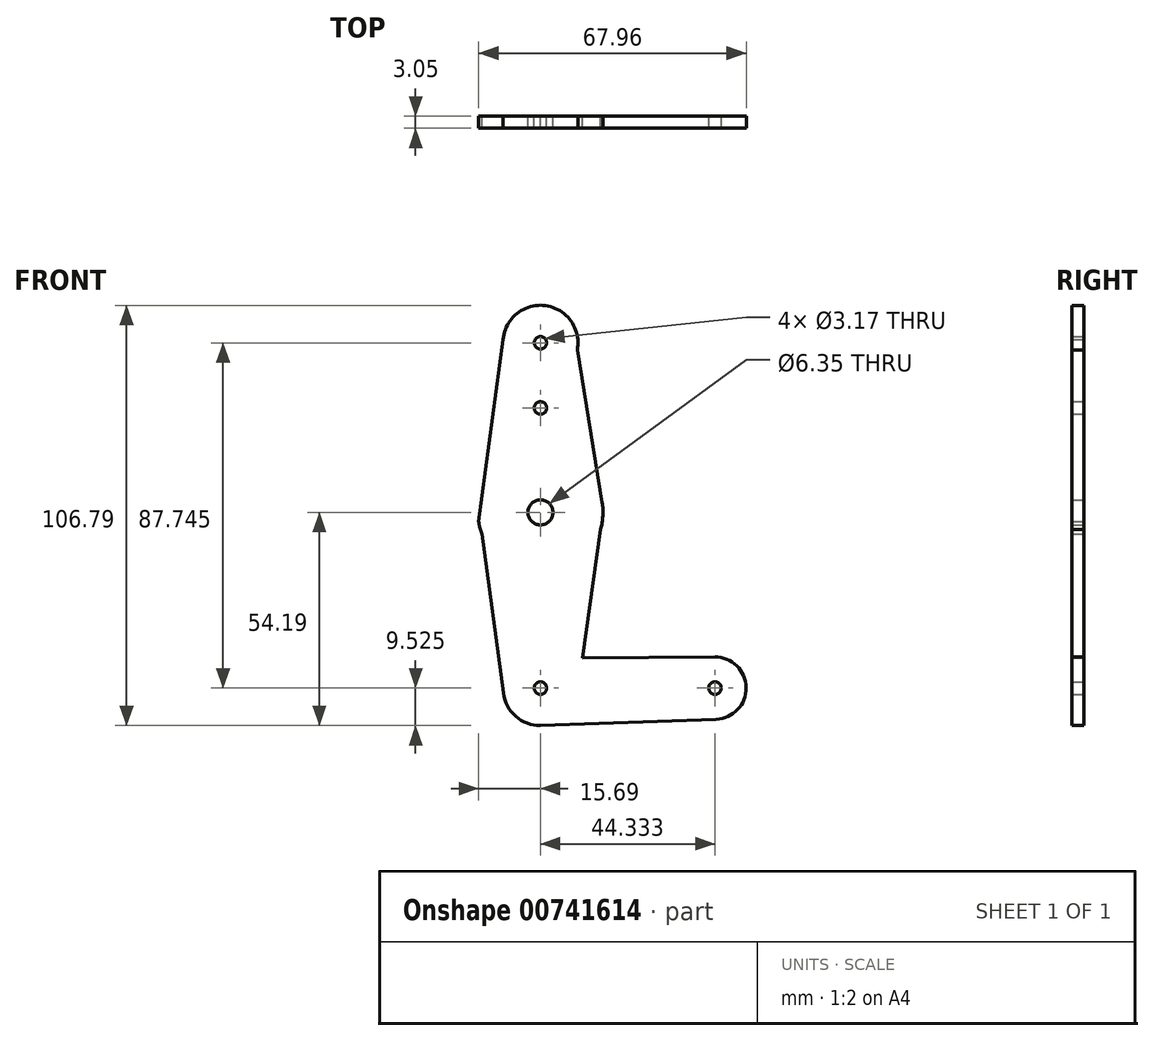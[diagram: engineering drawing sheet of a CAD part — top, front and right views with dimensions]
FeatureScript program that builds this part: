
annotation { "Feature Type Name" : "Feature", "Feature Type Description" : "" }
export const myFeature = defineFeature(function(context is Context, id is Id, definition is map)
    precondition{}
    {
        {
            var Q0;
            Q0=qCreatedBy(makeId("Front.planeOp"),FACE);
            var sketch = newSketch(context, id + "F0", { "sketchPlane" : qUnion([Q0])});
            skLineSegment(sketch, "E0", {"start": v(0, 43.08) * mm, "end": v(0, 0) * mm});
            skLineSegment(sketch, "E1", {"start": v(0, -44.66) * mm, "end": v(0, 0) * mm});
            skLineSegment(sketch, "E2", {"start": v(0, -44.66) * mm, "end": v(44.33, -44.66) * mm});
            skCircle(sketch, "E3", {"center": v(0, 43.08) * mm, "radius": 9.53 * mm});
            skCircle(sketch, "E4", {"center": v(0, 0) * mm, "radius": 15.88 * mm});
            skCircle(sketch, "E5", {"center": v(0, -44.66) * mm, "radius": 9.53 * mm});
            skCircle(sketch, "E6", {"center": v(44.33, -44.66) * mm, "radius": 7.94 * mm});
            skLineSegment(sketch, "E7", {"start": v(-9.5, 43.85) * mm, "end": v(-15.7, -2.38) * mm});
            skLineSegment(sketch, "E8", {"start": v(-14.9, -5.48) * mm, "end": v(-9.44, -45.94) * mm});
            skLineSegment(sketch, "E9", {"start": v(9.35, 41.25) * mm, "end": v(16.09, 0) * mm});
            skLineSegment(sketch, "E10", {"start": v(15.28, -4.32) * mm, "end": v(9.62, -44.66) * mm});
            skLineSegment(sketch, "E11", {"start": v(5.66, -37) * mm, "end": v(44.28, -36.73) * mm});
            skCircle(sketch, "E12", {"center": v(0, 0) * mm, "radius": 3.18 * mm});
            skCircle(sketch, "E13", {"center": v(0, 43.08) * mm, "radius": 1.59 * mm});
            skCircle(sketch, "E14", {"center": v(0, 26.53) * mm, "radius": 1.59 * mm});
            skCircle(sketch, "E15", {"center": v(0, -44.66) * mm, "radius": 1.59 * mm});
            skCircle(sketch, "E16", {"center": v(44.33, -44.66) * mm, "radius": 1.59 * mm});
            skLineSegment(sketch, "E17", {"start": v(0, -54.19) * mm, "end": v(44.62, -52.6) * mm});
            skSolve(sketch);
        }
        {
            var Q0;
            {var subQ3=sQuery(id+"F0.wireOp",EDGE,"E0");var subQ5=sQuery(id+"F0.wireOp",EDGE,"E3");var subQ7=makeQuery(id+"F0.imprint","INTERSECT",VERTEX,{"derivedFrom":[subQ3,subQ5]});Q0=makeQuery(id+"F0.imprint","IMPRINT",FACE,{"disambiguationData":[TD([[makeQuery(id+"F0.imprint","IMPRINT",EDGE,{"disambiguationData":[TD([[subQ7,-1.0]])],"derivedFrom":subQ3}),-1.0]])]});}
            var Q1;
            Q1=makeQuery(id+"F0.imprint","IMPRINT",FACE,{"disambiguationData":[TD([[makeQuery(id+"F0.imprint","IMPRINT",EDGE,{"derivedFrom":sQuery(id+"F0.wireOp",EDGE,"E13")}),-1.0]])]});
            var Q2;
            {var subQ3=sQuery(id+"F0.wireOp",EDGE,"E0");var subQ7=sQuery(id+"F0.wireOp",EDGE,"E3");var subQ9=makeQuery(id+"F0.imprint","INTERSECT",VERTEX,{"derivedFrom":[subQ3,subQ7]});Q2=makeQuery(id+"F0.imprint","IMPRINT",FACE,{"disambiguationData":[TD([[makeQuery(id+"F0.imprint","IMPRINT",EDGE,{"disambiguationData":[TD([[subQ9,-1.0]])],"derivedFrom":subQ3}),1.0]])]});}
            var Q3;
            {var subQ0=sQuery(id+"F0.wireOp",EDGE,"E4");var subQ5=sQuery(id+"F0.wireOp",EDGE,"E0");var subQ6=makeQuery(id+"F0.imprint","INTERSECT",VERTEX,{"derivedFrom":[subQ5,subQ0]});Q3=makeQuery(id+"F0.imprint","IMPRINT",FACE,{"disambiguationData":[TD([[makeQuery(id+"F0.imprint","IMPRINT",EDGE,{"disambiguationData":[TD([[subQ6,-1.0]])],"derivedFrom":subQ5}),1.0]])]});}
            var Q4;
            {var subQ1=sQuery(id+"F0.wireOp",EDGE,"E4");var subQ5=sQuery(id+"F0.wireOp",EDGE,"E0");var subQ6=makeQuery(id+"F0.imprint","INTERSECT",VERTEX,{"derivedFrom":[subQ5,subQ1]});Q4=makeQuery(id+"F0.imprint","IMPRINT",FACE,{"disambiguationData":[TD([[makeQuery(id+"F0.imprint","IMPRINT",EDGE,{"disambiguationData":[TD([[subQ6,-1.0]])],"derivedFrom":subQ5}),-1.0]])]});}
            var Q5;
            {var subQ5=sQuery(id+"F0.wireOp",EDGE,"E8");Q5=makeQuery(id+"F0.imprint","IMPRINT",FACE,{"disambiguationData":[TD([[makeQuery(id+"F0.imprint","IMPRINT",EDGE,{"derivedFrom":subQ5}),1.0]])]});}
            var Q6;
            {var subQ1=sQuery(id+"F0.wireOp",EDGE,"E5");var subQ3=sQuery(id+"F0.wireOp",EDGE,"E1");var subQ4=makeQuery(id+"F0.imprint","INTERSECT",VERTEX,{"derivedFrom":[subQ3,subQ1]});Q6=makeQuery(id+"F0.imprint","IMPRINT",FACE,{"disambiguationData":[TD([[makeQuery(id+"F0.imprint","IMPRINT",EDGE,{"disambiguationData":[TD([[subQ4,-1.0]])],"derivedFrom":subQ3}),-1.0]])]});}
            var Q7;
            {var subQ2=sQuery(id+"F0.wireOp",EDGE,"E1");var subQ6=sQuery(id+"F0.wireOp",EDGE,"E15");var subQ7=makeQuery(id+"F0.imprint","INTERSECT",VERTEX,{"derivedFrom":[subQ2,subQ6]});Q7=makeQuery(id+"F0.imprint","IMPRINT",FACE,{"disambiguationData":[TD([[makeQuery(id+"F0.imprint","IMPRINT",EDGE,{"disambiguationData":[TD([[subQ7,-1.0]])],"derivedFrom":subQ2}),-1.0]])]});}
            var Q8;
            {var subQ5=sQuery(id+"F0.wireOp",EDGE,"E1");var subQ7=sQuery(id+"F0.wireOp",EDGE,"E15");var subQ11=makeQuery(id+"F0.imprint","INTERSECT",VERTEX,{"derivedFrom":[subQ5,subQ7]});Q8=makeQuery(id+"F0.imprint","IMPRINT",FACE,{"disambiguationData":[TD([[makeQuery(id+"F0.imprint","IMPRINT",EDGE,{"disambiguationData":[TD([[subQ11,-1.0]])],"derivedFrom":subQ5}),1.0]])]});}
            var Q9;
            {var subQ0=sQuery(id+"F0.wireOp",EDGE,"E10");var subQ1=sQuery(id+"F0.wireOp",EDGE,"E2");var subQ2=makeQuery(id+"F0.imprint","INTERSECT",VERTEX,{"derivedFrom":[subQ1,subQ0]});Q9=makeQuery(id+"F0.imprint","IMPRINT",FACE,{"disambiguationData":[TD([[makeQuery(id+"F0.imprint","IMPRINT",EDGE,{"disambiguationData":[TD([[subQ2,1.0]])],"derivedFrom":subQ1}),1.0]])]});}
            var Q10;
            {var subQ0=sQuery(id+"F0.wireOp",EDGE,"E10");var subQ1=sQuery(id+"F0.wireOp",EDGE,"E2");var subQ2=makeQuery(id+"F0.imprint","INTERSECT",VERTEX,{"derivedFrom":[subQ1,subQ0]});Q10=makeQuery(id+"F0.imprint","IMPRINT",FACE,{"disambiguationData":[TD([[makeQuery(id+"F0.imprint","IMPRINT",EDGE,{"disambiguationData":[TD([[subQ2,-1.0]])],"derivedFrom":subQ1}),1.0]])]});}
            var Q11;
            {var subQ3=sQuery(id+"F0.wireOp",EDGE,"E2");var subQ8=makeQuery(id+"F0.imprint","INTERSECT",VERTEX,{"derivedFrom":[subQ3,sQuery(id+"F0.wireOp",EDGE,"E10")]});Q11=makeQuery(id+"F0.imprint","IMPRINT",FACE,{"disambiguationData":[TD([[makeQuery(id+"F0.imprint","IMPRINT",EDGE,{"disambiguationData":[TD([[subQ8,1.0]])],"derivedFrom":subQ3}),-1.0]])]});}
            var Q12;
            Q12=makeQuery(id+"F0.imprint","IMPRINT",FACE,{"disambiguationData":[TD([[makeQuery(id+"F0.imprint","IMPRINT",EDGE,{"derivedFrom":sQuery(id+"F0.wireOp",EDGE,"E16")}),-1.0]])]});
            extrude(context, id + "F1", {"entities" : qUnion([Q0, Q1, Q2, Q3, Q4, Q5, Q6, Q7, Q8, Q9, Q10, Q11, Q12]), "depth" : 3.05 * mm, "offsetDistance" : 25.4 * mm});
        }
    });
